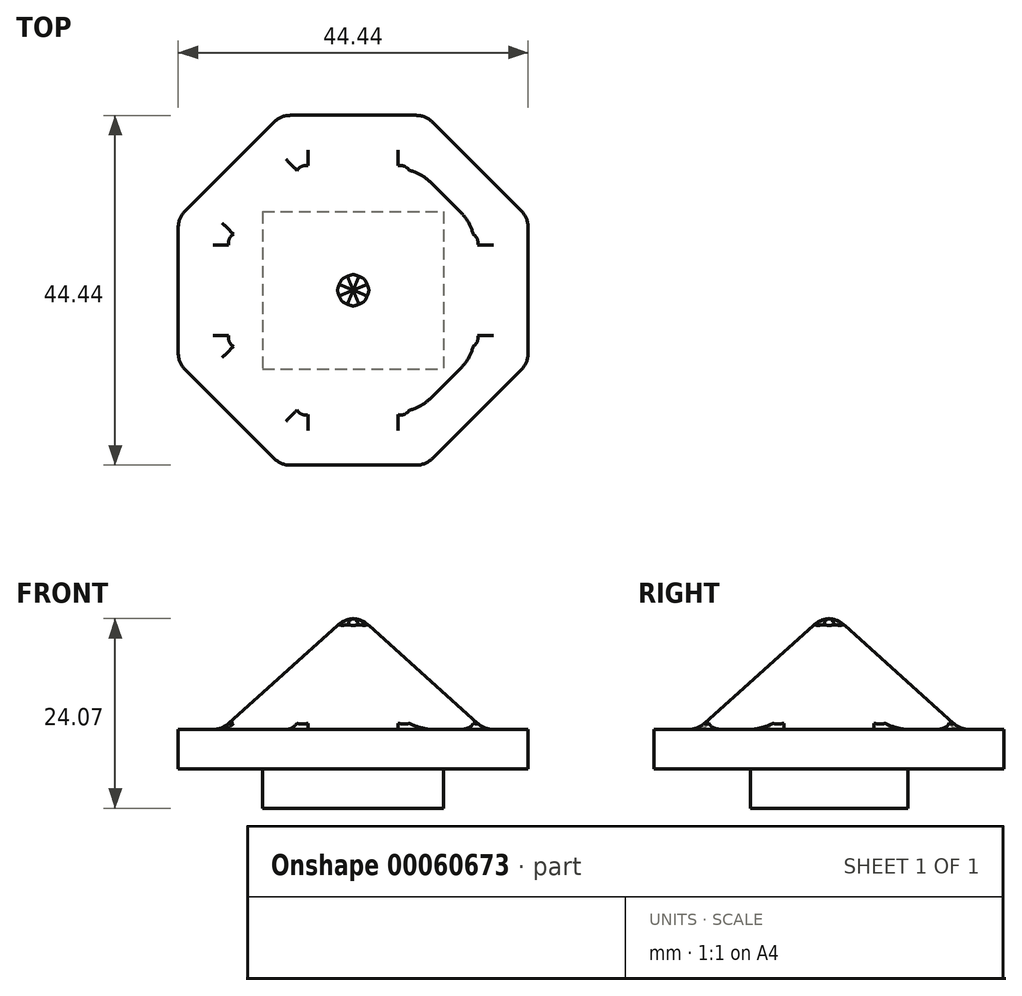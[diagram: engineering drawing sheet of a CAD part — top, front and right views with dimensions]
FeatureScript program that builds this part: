
annotation { "Feature Type Name" : "Feature", "Feature Type Description" : "" }
export const myFeature = defineFeature(function(context is Context, id is Id, definition is map)
    precondition{}
    {
        {
            var Q0;
            Q0=qCreatedBy(makeId("Top.planeOp"),FACE);
            var sketch = newSketch(context, id + "F0", { "sketchPlane" : qUnion([Q0])});
            skLineSegment(sketch, "E0.bottom", {"start": v(-11.5, 10) * mm, "end": v(11.5, 10) * mm});
            skLineSegment(sketch, "E0.top", {"start": v(-11.5, -10) * mm, "end": v(11.5, -10) * mm});
            skLineSegment(sketch, "E0.left", {"start": v(-11.5, 10) * mm, "end": v(-11.5, -10) * mm});
            skLineSegment(sketch, "E0.right", {"start": v(11.5, 10) * mm, "end": v(11.5, -10) * mm});
            skSolve(sketch);
        }
        {
            var Q0;
            Q0 = qSketchRegion(id + "F0", true);
            extrude(context, id + "F1", {"entities" : qUnion([Q0]), "depth" : 5 * mm});
        }
        {
            var Q0;
            Q0=makeQuery(id+"F1.opExtrude","CAP_FACE",FACE,{"disambiguationData":[OSD([sQuery(id+"F0.wireOp",EDGE,"E0.bottom"),sQuery(id+"F0.wireOp",EDGE,"E0.top"),sQuery(id+"F0.wireOp",EDGE,"E0.left"),sQuery(id+"F0.wireOp",EDGE,"E0.right")])],"isStart":false});
            var sketch = newSketch(context, id + "F2", { "sketchPlane" : qUnion([Q0])});
            skCircle(sketch, "E1.cCircle", {"center": v(0, 0) * mm, "radius": 22.22 * mm, "construction": true});
            skLineSegment(sketch, "E1.0", {"start": v(22.22, 9.2) * mm, "end": v(22.22, -9.2) * mm});
            skLineSegment(sketch, "E1.1", {"start": v(22.22, -9.2) * mm, "end": v(9.2, -22.22) * mm});
            skLineSegment(sketch, "E1.2", {"start": v(9.2, -22.22) * mm, "end": v(-9.2, -22.22) * mm});
            skLineSegment(sketch, "E1.3", {"start": v(-9.2, -22.22) * mm, "end": v(-22.22, -9.2) * mm});
            skLineSegment(sketch, "E1.4", {"start": v(-22.22, -9.2) * mm, "end": v(-22.22, 9.2) * mm});
            skLineSegment(sketch, "E1.5", {"start": v(-22.22, 9.2) * mm, "end": v(-9.2, 22.22) * mm});
            skLineSegment(sketch, "E1.6", {"start": v(-9.2, 22.22) * mm, "end": v(9.2, 22.22) * mm});
            skLineSegment(sketch, "E1.7", {"start": v(9.2, 22.22) * mm, "end": v(22.22, 9.2) * mm});
            skPoint(sketch, "E1.0.midPoint", {"position": v(22.22, 0) * mm});
            skSolve(sketch);
        }
        {
            var Q0;
            Q0 = qSketchRegion(id + "F2", true);
            extrude(context, id + "F3", {"entities" : qUnion([Q0]), "operationType" : NewBodyOperationType.ADD, "depth" : 5 * mm});
        }
        {
            var Q0;
            Q0=makeQuery(id+"F2.imprint","IMPRINT",FACE,{"disambiguationData":[TD([[makeQuery(id+"F2.imprint","IMPRINT",EDGE,{"derivedFrom":makeQuery(id+"F1.opExtrude","CAP_EDGE",EDGE,{"disambiguationData":[OSD([sQuery(id+"F0.wireOp",EDGE,"E0.bottom")])],"isStart":false})}),-1.0]])]});
            cPlane(context, id + "F4", {"entities" : qUnion([Q0]), "cplaneType" : CPlaneType.OFFSET, "offset" : 20 * mm, "width" : 150 * mm, "height" : 150 * mm});
        }
        {
            var Q0;
            Q0=qCreatedBy(id+"F4.planeOp",FACE);
            var sketch = newSketch(context, id + "F5", { "sketchPlane" : qUnion([Q0])});
            skPoint(sketch, "E2.0", {"position": v(0, 0) * mm});
            skSolve(sketch);
        }
        {
            var Q1;
            Q1=sQuery(id+"F5.wireOp",VERTEX,"E2.0");
            var Q2;
            Q2 = qSketchRegion(id + "F2", true);
            loft(context, id + "F6", {"operationType" : NewBodyOperationType.ADD, "sheetProfilesArray" : [{ "sheetProfileEntities" : qUnion([Q1]) }, { "sheetProfileEntities" : qUnion([Q2]) }]});
        }
        {
            var Q0;
            Q0=makeQuery(id+"F6.opLoft","SWEPT_EDGE",EDGE,{"disambiguationData":[OSD([sQuery(id+"F2.wireOp",EDGE,"E1.0"),sQuery(id+"F2.wireOp",EDGE,"E1.1"),sQuery(id+"F5.wireOp",VERTEX,"E2.0")])]});
            var Q1;
            Q1=makeQuery(id+"F6.opLoft","SWEPT_FACE",FACE,{"disambiguationData":[OSD([sQuery(id+"F2.wireOp",EDGE,"E1.0"),sQuery(id+"F2.wireOp",EDGE,"E1.1"),sQuery(id+"F2.wireOp",EDGE,"E1.7")])]});
            var Q2;
            Q2=makeQuery(id+"F6.opLoft","SWEPT_FACE",FACE,{"disambiguationData":[OSD([sQuery(id+"F2.wireOp",EDGE,"E1.2"),sQuery(id+"F2.wireOp",EDGE,"E1.3"),sQuery(id+"F2.wireOp",EDGE,"E1.4")])]});
            var Q3;
            Q3=makeQuery(id+"F6.opLoft","SWEPT_FACE",FACE,{"disambiguationData":[OSD([sQuery(id+"F2.wireOp",EDGE,"E1.1"),sQuery(id+"F2.wireOp",EDGE,"E1.2"),sQuery(id+"F2.wireOp",EDGE,"E1.3")])]});
            var Q4;
            Q4=makeQuery(id+"F6.opLoft","SWEPT_FACE",FACE,{"disambiguationData":[OSD([sQuery(id+"F2.wireOp",EDGE,"E1.3"),sQuery(id+"F2.wireOp",EDGE,"E1.4"),sQuery(id+"F2.wireOp",EDGE,"E1.5")])]});
            var Q5;
            Q5=makeQuery(id+"F6.opLoft","SWEPT_FACE",FACE,{"disambiguationData":[OSD([sQuery(id+"F2.wireOp",EDGE,"E1.4"),sQuery(id+"F2.wireOp",EDGE,"E1.5"),sQuery(id+"F2.wireOp",EDGE,"E1.6")])]});
            var Q6;
            Q6=makeQuery(id+"F6.opLoft","SWEPT_FACE",FACE,{"disambiguationData":[OSD([sQuery(id+"F2.wireOp",EDGE,"E1.5"),sQuery(id+"F2.wireOp",EDGE,"E1.6"),sQuery(id+"F2.wireOp",EDGE,"E1.7")])]});
            var Q7;
            Q7=makeQuery(id+"F6.opLoft","SWEPT_EDGE",EDGE,{"disambiguationData":[OSD([sQuery(id+"F2.wireOp",EDGE,"E1.6"),sQuery(id+"F2.wireOp",EDGE,"E1.7"),sQuery(id+"F5.wireOp",VERTEX,"E2.0")])]});
            var Q8;
            Q8=makeQuery(id+"F3.opExtrude","SWEPT_EDGE",EDGE,{"disambiguationData":[OSD([sQuery(id+"F2.wireOp",EDGE,"E1.2"),sQuery(id+"F2.wireOp",EDGE,"E1.3")])]});
            var Q9;
            Q9=makeQuery(id+"F3.opExtrude","SWEPT_EDGE",EDGE,{"disambiguationData":[OSD([sQuery(id+"F2.wireOp",EDGE,"E1.1"),sQuery(id+"F2.wireOp",EDGE,"E1.2")])]});
            var Q10;
            Q10=makeQuery(id+"F3.opExtrude","SWEPT_EDGE",EDGE,{"disambiguationData":[OSD([sQuery(id+"F2.wireOp",EDGE,"E1.0"),sQuery(id+"F2.wireOp",EDGE,"E1.1")])]});
            var Q11;
            Q11=makeQuery(id+"F3.opExtrude","SWEPT_EDGE",EDGE,{"disambiguationData":[OSD([sQuery(id+"F2.wireOp",EDGE,"E1.0"),sQuery(id+"F2.wireOp",EDGE,"E1.7")])]});
            var Q12;
            Q12=makeQuery(id+"F3.opExtrude","SWEPT_EDGE",EDGE,{"disambiguationData":[OSD([sQuery(id+"F2.wireOp",EDGE,"E1.6"),sQuery(id+"F2.wireOp",EDGE,"E1.7")])]});
            var Q13;
            Q13=makeQuery(id+"F3.opExtrude","SWEPT_EDGE",EDGE,{"disambiguationData":[OSD([sQuery(id+"F2.wireOp",EDGE,"E1.5"),sQuery(id+"F2.wireOp",EDGE,"E1.6")])]});
            var Q14;
            Q14=makeQuery(id+"F3.opExtrude","SWEPT_EDGE",EDGE,{"disambiguationData":[OSD([sQuery(id+"F2.wireOp",EDGE,"E1.4"),sQuery(id+"F2.wireOp",EDGE,"E1.5")])]});
            var Q15;
            Q15=makeQuery(id+"F3.opExtrude","SWEPT_EDGE",EDGE,{"disambiguationData":[OSD([sQuery(id+"F2.wireOp",EDGE,"E1.3"),sQuery(id+"F2.wireOp",EDGE,"E1.4")])]});
            fillet(context, id + "F7", {"entities" : qUnion([Q0, Q1, Q2, Q3, Q4, Q5, Q6, Q7, Q8, Q9, Q10, Q11, Q12, Q13, Q14, Q15]), "radius" : 3 * mm, "tangentPropagation" : true, "allowEdgeOverflow" : false});
        }
    });
